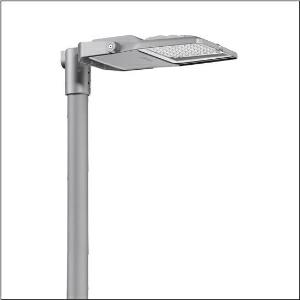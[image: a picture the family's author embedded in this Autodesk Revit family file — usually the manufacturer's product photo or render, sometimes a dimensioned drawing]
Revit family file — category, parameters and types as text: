
# Revit family: floodlight_fl_21_iq_mini___pl33t_5xa7771d2f3a_c3c2
name_source: partatom
category: Lighting Fixtures
units: mm (PartAtom-declared; Revit-internal decimal feet)

## family parameters
Cut with Voids When Loaded = No
Host = Face
Light Source = No
Part Type = Normal
Room Calculation Point = No
Round Connector Dimension = Use Diameter
Shared = No

## types (1)
- --- (1 x LED, 17620 lm, 143 W, 3000K)
    Apparent Load = 143 VA
    CIE Flux Codes = 26 75 99 100 100
    Color Rendering = 70
    Color Temperature = 3000K
    Default Elevation = 1800 mm
    Description = Floodlight FL 21 iQ mini, floodlight, primary light control with lens, of PMMA, primary optical cover: protective disc, of toughened safety glass, transparent, light distribution: PL33T, light emission: direct distribution, installation type: surface-mounted, LED, High Power LED, rated luminous flux: 17.620lm, luminous efficacy: 123lm/W, light colour: 730, colour temperature: 3000K, control: Auto-Match, Temp-Guard, Lumen-Switch, Night-Set, Smart-Wire, Light-Fading, Desk-Remote (wireless, voltage-free reading and setting of iQ features in the workshop via application-optimized NFC function/RFID function), optimised constant luminous flux control (CLO 2.0), with terminal, 6-pole, mains connection: 220..240V, AC, 50/60Hz, start of lifetime: 143W, end of service life: 152W, reduction: 61W, luminaire housing, of diecast aluminium, powder-coated, Siteco® metallic grey (DB 702S), corrosivity category C5 mid according to DIN EN ISO 12944, sealing non-destructively replaceable, please order mast flange separately, mast bracket, of steel, galvanised, powder-coated, Siteco® metallic grey (DB 702S), protection rating (complete): IP66, insulation class (complete): insulation class II (safety insulation), certification: CE, ENEC, VDE, protection symbol: D, impact resistance: IK08, permissible operating ambient temperature: -40..+40°C, permissible operating ambient temperature for outdoor applications: -40..+50°C, standard: DIN EN 12944, LABS conformity tested according to VDMA 24364:2018-05, packaging unit: 1 piece

Light Distribution: PL33T
    Height = 70 mm
    Lamp = 1 x LED
    Lamp Light Flux = 17620 lm
    Lamp Power = 143 W
    Lamp count = 1
    Length = 485 mm
    Luminous efficacy = 123 lm/W
    Manufacturer = Siteco
    ModVariant = No
    Model = 5XA7771D2F3A
    Number of Poles = 1
    OnlyDefault = Yes
    Power Factor = 1
    Product Name = Floodlight FL 21 iQ mini | PL33T
    Product group = floodlight | pylon annexe
    ProductGroupID = 6200
    Protection Class = Protection class II
    Protection Degree = IP 66
    RLX_Detail_Level = 1
    RLX_Emergency_Light_Flux = 0 lm
    RLX_Emergency_Type = 0
    RLX_Emergency_Type_DB = No
    RlxData = <blob elided: 101493 chars, md5=11f326a5>
    Socket = socket
    Standby Power = 0 W
    System Light Flux = 17620 lm
    System Power = 143 W
    Type Comments = factory setting: luminous flux: 100 % | dim-lin: 254 | 730 mA
    Type Image = l_1007125.jpg
    URL = http://relux.com
    VarID = @adj_081681
    Voltage = 0 V
    Weight = 0.00 kg
    Width = 337 mm

## geometry (parser evidence)
native form markers: Blend x4, Sweep x12
no freeform markers — native parametric forms only
